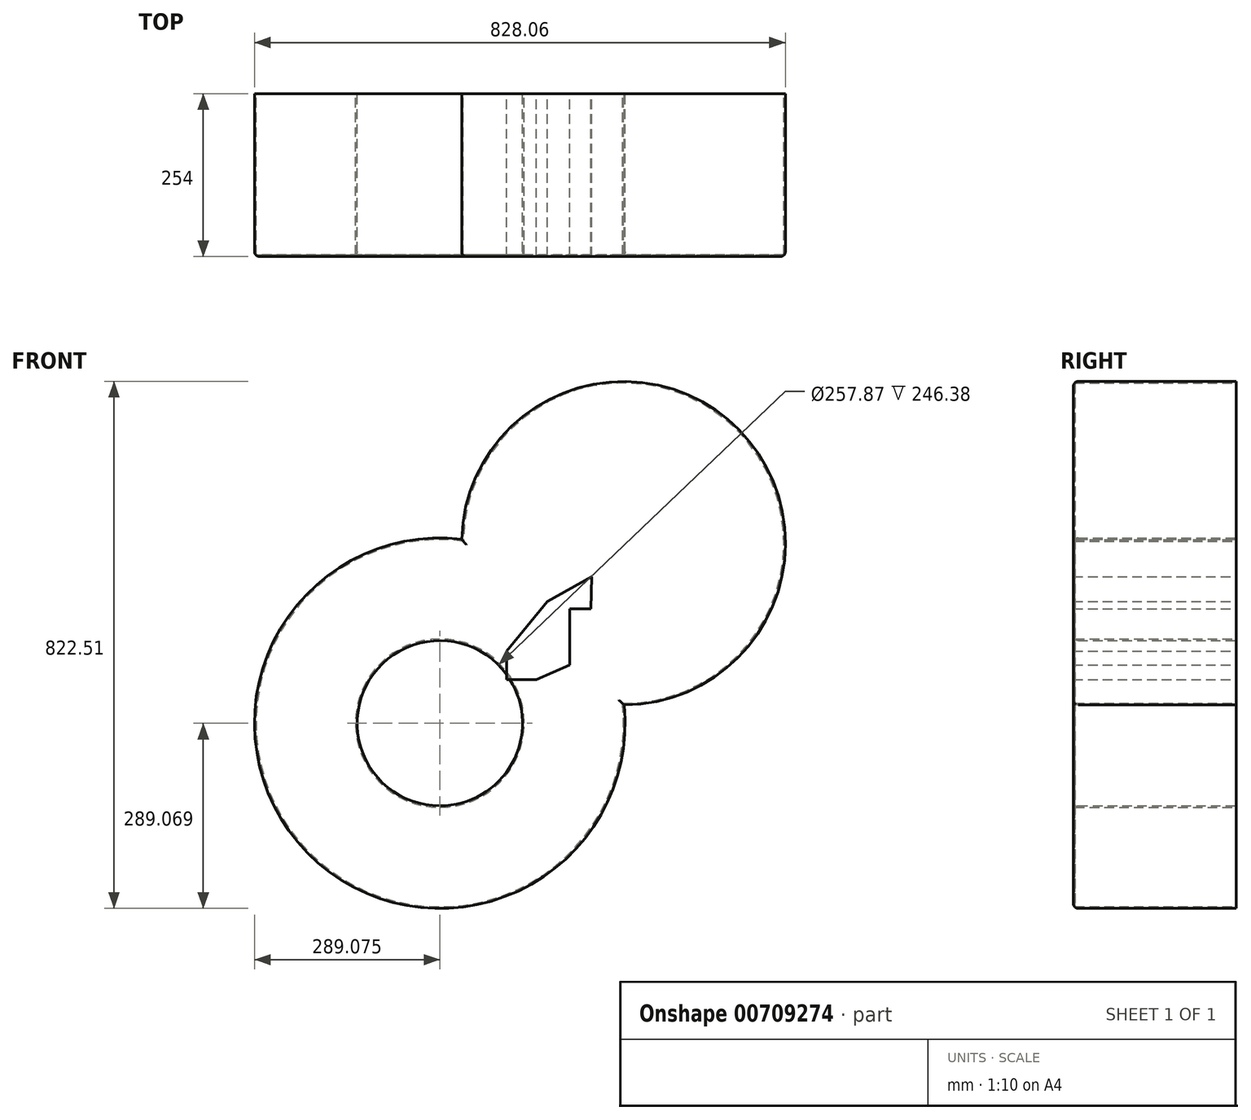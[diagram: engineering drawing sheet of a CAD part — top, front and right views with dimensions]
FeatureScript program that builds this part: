
annotation { "Feature Type Name" : "Feature", "Feature Type Description" : "" }
export const myFeature = defineFeature(function(context is Context, id is Id, definition is map)
    precondition{}
    {
        {
            var Q0;
            Q0=qCreatedBy(makeId("Front.planeOp"),FACE);
            var sketch = newSketch(context, id + "F0", { "sketchPlane" : qUnion([Q0])});
            skLineSegment(sketch, "E0.bottom", {"start": v(-227.99, -36.3) * mm, "end": v(-182.02, -36.3) * mm});
            skLineSegment(sketch, "E0.top", {"start": v(-227.99, -80.49) * mm, "end": v(-182.02, -80.49) * mm});
            skLineSegment(sketch, "E0.left", {"start": v(-227.99, -36.3) * mm, "end": v(-227.99, -80.49) * mm});
            skLineSegment(sketch, "E0.right", {"start": v(-182.02, -36.3) * mm, "end": v(-182.02, -80.49) * mm});
            skLineSegment(sketch, "E1", {"start": v(-227.99, -36.3) * mm, "end": v(-164.27, 41.11) * mm});
            skLineSegment(sketch, "E2", {"start": v(-164.27, 41.11) * mm, "end": v(-129.8, 30.17) * mm});
            skLineSegment(sketch, "E3", {"start": v(-129.8, 30.17) * mm, "end": v(-182.02, -36.3) * mm});
            skLineSegment(sketch, "E4", {"start": v(-129.8, 30.17) * mm, "end": v(-129.8, -57.87) * mm});
            skLineSegment(sketch, "E5", {"start": v(-182.02, -80.49) * mm, "end": v(-129.8, -57.87) * mm});
            skLineSegment(sketch, "E6", {"start": v(-96.37, 30.17) * mm, "end": v(-129.8, 30.17) * mm});
            skLineSegment(sketch, "E7", {"start": v(-164.27, 41.11) * mm, "end": v(-95.32, 79.82) * mm});
            skLineSegment(sketch, "E8", {"start": v(-96.37, 30.17) * mm, "end": v(-95.32, 79.82) * mm});
            skSolve(sketch);
        }
        {
            var Q0;
            Q0=makeQuery(id+"F0.imprint","IMPRINT",FACE,{"disambiguationData":[TD([[makeQuery(id+"F0.imprint","IMPRINT",EDGE,{"derivedFrom":sQuery(id+"F0.wireOp",EDGE,"E0.bottom")}),1.0]])]});
            var sketch = newSketch(context, id + "F1", { "sketchPlane" : qUnion([Q0])});
            skCircle(sketch, "E9", {"center": v(-332.23, -148.6) * mm, "radius": 128.94 * mm});
            skCircle(sketch, "E10", {"center": v(-332.23, -148.6) * mm, "radius": 289.07 * mm});
            skCircle(sketch, "E11", {"center": v(-45.75, 132.34) * mm, "radius": 252.52 * mm});
            skSolve(sketch);
        }
        {
            var Q0;
            Q0 = qSketchRegion(id + "F0", true);
            var Q1;
            Q1 = qSketchRegion(id + "F1", true);
            extrude(context, id + "F2", {"entities" : qUnion([Q0, Q1]), "depth" : 254 * mm, "offsetDistance" : 25.4 * mm});
        }
        {
            var Q0;
            Q0=makeQuery(id+"F2.opExtrude","CAP_FACE",FACE,{"disambiguationData":[OSD([sQuery(id+"F1.wireOp",EDGE,"E9"),sQuery(id+"F1.wireOp",EDGE,"E10"),sQuery(id+"F1.wireOp",EDGE,"E11")])],"isStart":true});
            shell(context, id + "F3", {"entities" : qUnion([Q0]), "thickness" : 2.54 * mm});
        }
        {
            var Q0;
            Q0=makeQuery(id+"F2.opExtrude","CAP_FACE",FACE,{"disambiguationData":[OSD([sQuery(id+"F1.wireOp",EDGE,"E9"),sQuery(id+"F1.wireOp",EDGE,"E10"),sQuery(id+"F1.wireOp",EDGE,"E11")])],"isStart":false});
            fillet(context, id + "F4", {"entities" : qUnion([Q0]), "radius" : 7.62 * mm, "tangentPropagation" : true, "allowEdgeOverflow" : false});
        }
    });
